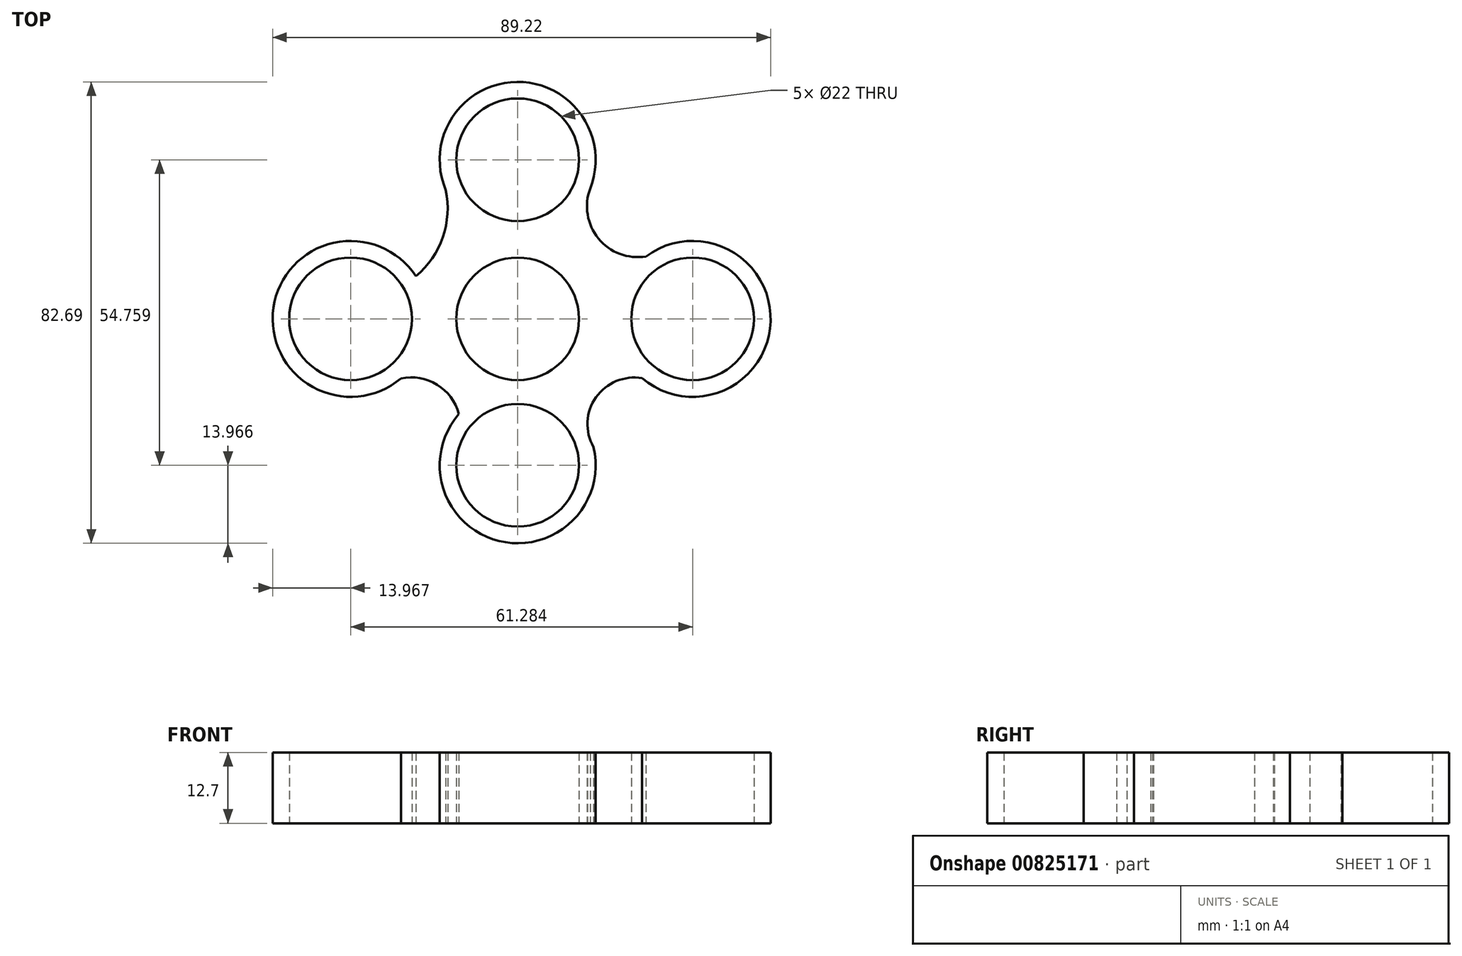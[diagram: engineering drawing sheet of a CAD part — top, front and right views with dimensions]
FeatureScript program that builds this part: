
annotation { "Feature Type Name" : "Feature", "Feature Type Description" : "" }
export const myFeature = defineFeature(function(context is Context, id is Id, definition is map)
    precondition{}
    {
        {
            var Q0;
            Q0=qCreatedBy(makeId("Top.planeOp"),FACE);
            var sketch = newSketch(context, id + "F0", { "sketchPlane" : qUnion([Q0])});
            skCircle(sketch, "E0", {"center": v(0, 0) * mm, "radius": 44.45 * mm});
            skCircle(sketch, "E1", {"center": v(0, 0) * mm, "radius": 11 * mm});
            skCircle(sketch, "E2", {"center": v(0, 28.51) * mm, "radius": 11 * mm});
            skCircle(sketch, "E3", {"center": v(-29.93, 0) * mm, "radius": 11 * mm});
            skCircle(sketch, "E4", {"center": v(0, -26.24) * mm, "radius": 11 * mm});
            skCircle(sketch, "E5", {"center": v(31.35, 0) * mm, "radius": 11 * mm});
            skCircle(sketch, "E6", {"center": v(-29.93, 0) * mm, "radius": 13.97 * mm});
            skCircle(sketch, "E7", {"center": v(0, -26.24) * mm, "radius": 13.97 * mm});
            skCircle(sketch, "E8", {"center": v(31.35, 0) * mm, "radius": 13.97 * mm});
            skCircle(sketch, "E9", {"center": v(0, 28.51) * mm, "radius": 13.97 * mm});
            skCircle(sketch, "E10", {"center": v(0, 0) * mm, "radius": 13.97 * mm});
            skArc(sketch, "E11", {"start": v(-18.25, 7.66) * mm, "mid": v(-13.42, 14.65) * mm, "end": v(-12.9, 23.13) * mm});
            skArc(sketch, "E12", {"start": v(-10.52, -17.06) * mm, "mid": v(-14.45, -11.8) * mm, "end": v(-20.91, -10.67) * mm});
            skArc(sketch, "E13", {"start": v(13, 23.38) * mm, "mid": v(14.48, 14.4) * mm, "end": v(22.99, 11.19) * mm});
            skArc(sketch, "E14", {"start": v(22.28, -10.63) * mm, "mid": v(14.03, -14.06) * mm, "end": v(13.58, -22.98) * mm});
            skSolve(sketch);
        }
        {
            var Q0;
            Q0=makeQuery(id+"F0.imprint","IMPRINT",FACE,{"disambiguationData":[TD([[makeQuery(id+"F0.imprint","IMPRINT",EDGE,{"derivedFrom":sQuery(id+"F0.wireOp",EDGE,"E2")}),-1.0]])]});
            var Q1;
            {var subQ10=sQuery(id+"F0.wireOp",EDGE,"E11");Q1=makeQuery(id+"F0.imprint","IMPRINT",FACE,{"disambiguationData":[TD([[makeQuery(id+"F0.imprint","IMPRINT",EDGE,{"derivedFrom":subQ10}),-1.0]])]});}
            var Q2;
            Q2=makeQuery(id+"F0.imprint","IMPRINT",FACE,{"disambiguationData":[TD([[makeQuery(id+"F0.imprint","IMPRINT",EDGE,{"derivedFrom":sQuery(id+"F0.wireOp",EDGE,"E5")}),-1.0]])]});
            var Q3;
            Q3=makeQuery(id+"F0.imprint","IMPRINT",FACE,{"disambiguationData":[TD([[makeQuery(id+"F0.imprint","IMPRINT",EDGE,{"derivedFrom":sQuery(id+"F0.wireOp",EDGE,"E3")}),-1.0]])]});
            var Q4;
            Q4=makeQuery(id+"F0.imprint","IMPRINT",FACE,{"disambiguationData":[TD([[makeQuery(id+"F0.imprint","IMPRINT",EDGE,{"derivedFrom":sQuery(id+"F0.wireOp",EDGE,"E4")}),-1.0]])]});
            var Q5;
            {var subQ0=sQuery(id+"F0.wireOp",EDGE,"E10");var subQ1=sQuery(id+"F0.wireOp",EDGE,"E7");var subQ2=makeQuery(id+"F0.imprint","INTERSECT",VERTEX,{"disambiguationData":[OD(0.0)],"derivedFrom":[subQ1,subQ0]});Q5=makeQuery(id+"F0.imprint","IMPRINT",FACE,{"disambiguationData":[TD([[makeQuery(id+"F0.imprint","IMPRINT",EDGE,{"disambiguationData":[TD([[subQ2,-1.0]])],"derivedFrom":subQ1}),1.0]])]});}
            var Q6;
            Q6=makeQuery(id+"F0.imprint","IMPRINT",FACE,{"disambiguationData":[TD([[makeQuery(id+"F0.imprint","IMPRINT",EDGE,{"derivedFrom":sQuery(id+"F0.wireOp",EDGE,"E1")}),-1.0]])]});
            var Q7;
            {var subQ0=sQuery(id+"F0.wireOp",EDGE,"E8");var subQ1=sQuery(id+"F0.wireOp",EDGE,"E0");var subQ2=makeQuery(id+"F0.imprint","INTERSECT",VERTEX,{"disambiguationData":[OD(0.0)],"derivedFrom":[subQ1,subQ0]});Q7=makeQuery(id+"F0.imprint","IMPRINT",FACE,{"disambiguationData":[TD([[makeQuery(id+"F0.imprint","IMPRINT",EDGE,{"disambiguationData":[TD([[subQ2,1.0]])],"derivedFrom":subQ1}),-1.0]])]});}
            extrude(context, id + "F1", {"entities" : qUnion([Q0, Q1, Q2, Q3, Q4, Q5, Q6, Q7]), "depth" : 12.7 * mm, "offsetDistance" : 25.4 * mm});
        }
    });
